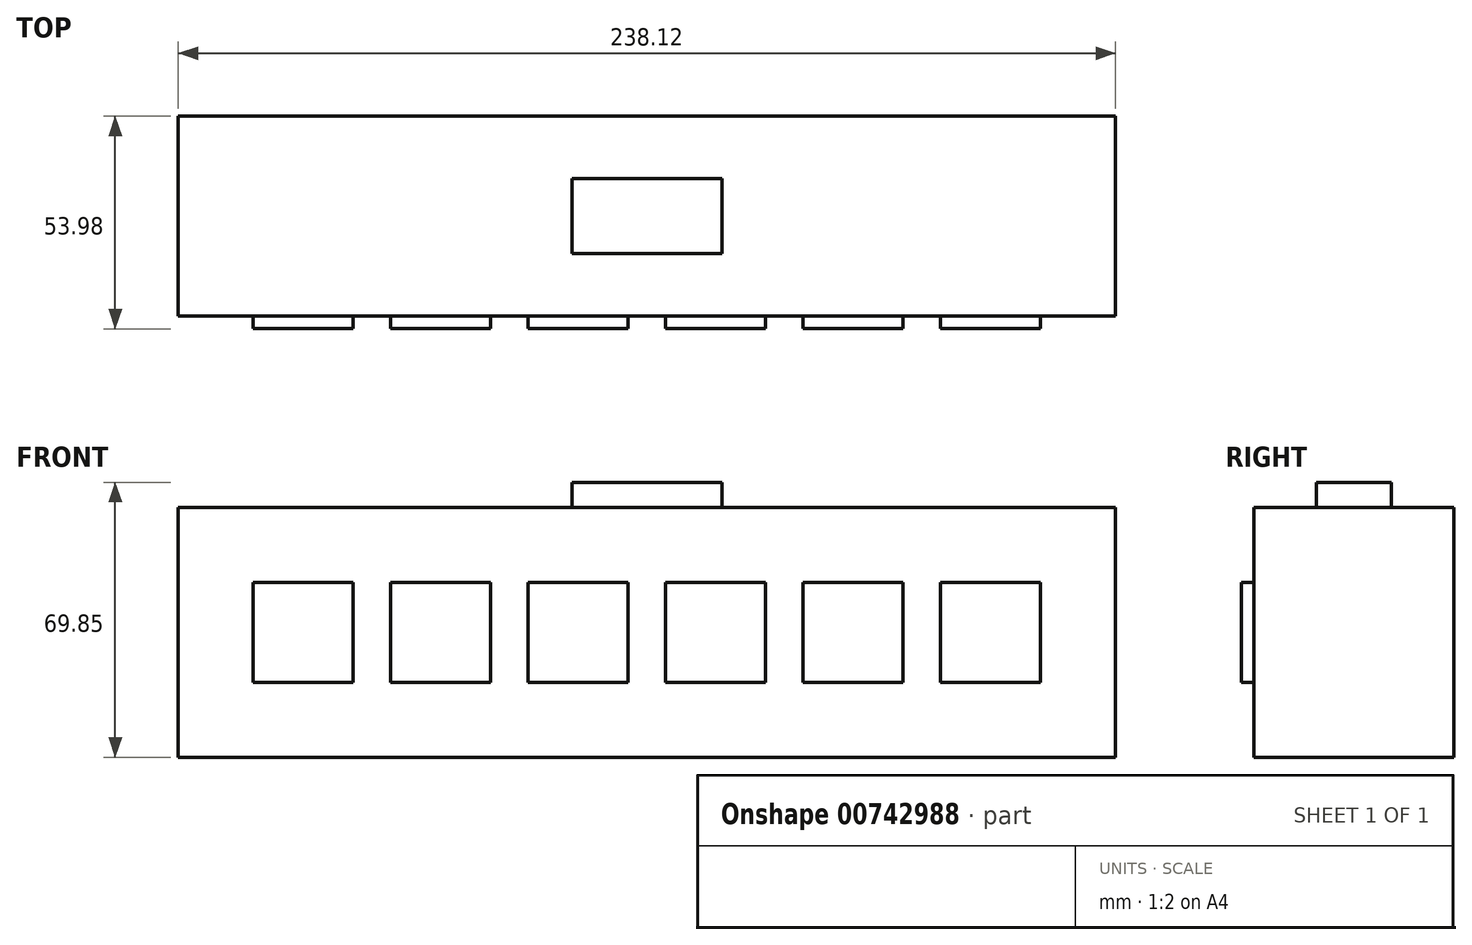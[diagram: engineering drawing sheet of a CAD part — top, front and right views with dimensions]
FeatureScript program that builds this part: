
annotation { "Feature Type Name" : "Feature", "Feature Type Description" : "" }
export const myFeature = defineFeature(function(context is Context, id is Id, definition is map)
    precondition{}
    {
        {
            var Q0;
            Q0=qCreatedBy(makeId("Front.planeOp"),FACE);
            var sketch = newSketch(context, id + "F0", { "sketchPlane" : qUnion([Q0])});
            skLineSegment(sketch, "E0.bottom", {"start": v(119.06, 31.75) * mm, "end": v(-119.06, 31.75) * mm});
            skLineSegment(sketch, "E0.top", {"start": v(119.06, -31.75) * mm, "end": v(-119.06, -31.75) * mm});
            skLineSegment(sketch, "E0.left", {"start": v(119.06, 31.75) * mm, "end": v(119.06, -31.75) * mm});
            skLineSegment(sketch, "E0.right", {"start": v(-119.06, 31.75) * mm, "end": v(-119.06, -31.75) * mm});
            skPoint(sketch, "E0.middle", {"position": v(0, 0) * mm});
            skSolve(sketch);
        }
        {
            var Q0;
            Q0=makeQuery(id+"F0.imprint","IMPRINT",FACE,{"disambiguationData":[TD([[makeQuery(id+"F0.imprint","IMPRINT",EDGE,{"derivedFrom":sQuery(id+"F0.wireOp",EDGE,"E0.bottom")}),1.0]])]});
            extrude(context, id + "F1", {"entities" : qUnion([Q0]), "depth" : 50.8 * mm, "offsetDistance" : 25.4 * mm});
        }
        {
            var Q0;
            Q0=makeQuery(id+"F1.opExtrude","CAP_FACE",FACE,{"disambiguationData":[OSD([sQuery(id+"F0.wireOp",EDGE,"E0.bottom"),sQuery(id+"F0.wireOp",EDGE,"E0.top"),sQuery(id+"F0.wireOp",EDGE,"E0.left"),sQuery(id+"F0.wireOp",EDGE,"E0.right")])],"isStart":false});
            var sketch = newSketch(context, id + "F2", { "sketchPlane" : qUnion([Q0])});
            skLineSegment(sketch, "E1", {"start": v(-119.06, 0) * mm, "end": v(-100.01, 0) * mm});
            skLineSegment(sketch, "E2", {"start": v(-100.01, 0) * mm, "end": v(-87.31, 0) * mm});
            skLineSegment(sketch, "E3", {"start": v(-87.31, 0) * mm, "end": v(-52.39, 0) * mm});
            skLineSegment(sketch, "E4", {"start": v(-52.39, 0) * mm, "end": v(-17.46, 0) * mm});
            skLineSegment(sketch, "E5", {"start": v(-17.46, 0) * mm, "end": v(17.46, 0) * mm});
            skLineSegment(sketch, "E6", {"start": v(17.46, 0) * mm, "end": v(52.39, 0) * mm});
            skLineSegment(sketch, "E7", {"start": v(52.39, 0) * mm, "end": v(87.31, 0) * mm});
            skLineSegment(sketch, "E8", {"start": v(87.31, 0) * mm, "end": v(100.01, 0) * mm});
            skLineSegment(sketch, "E9.bottom", {"start": v(-100.01, 12.7) * mm, "end": v(-74.61, 12.7) * mm});
            skLineSegment(sketch, "E9.top", {"start": v(-100.01, -12.7) * mm, "end": v(-74.61, -12.7) * mm});
            skLineSegment(sketch, "E9.left", {"start": v(-100.01, 12.7) * mm, "end": v(-100.01, -12.7) * mm});
            skLineSegment(sketch, "E9.right", {"start": v(-74.61, 12.7) * mm, "end": v(-74.61, -12.7) * mm});
            skPoint(sketch, "E9.middle", {"position": v(-87.31, 0) * mm});
            skLineSegment(sketch, "E10.bottom", {"start": v(-65.09, 12.7) * mm, "end": v(-39.69, 12.7) * mm});
            skLineSegment(sketch, "E10.top", {"start": v(-65.09, -12.7) * mm, "end": v(-39.69, -12.7) * mm});
            skLineSegment(sketch, "E10.left", {"start": v(-65.09, 12.7) * mm, "end": v(-65.09, -12.7) * mm});
            skLineSegment(sketch, "E10.right", {"start": v(-39.69, 12.7) * mm, "end": v(-39.69, -12.7) * mm});
            skPoint(sketch, "E10.middle", {"position": v(-52.39, 0) * mm});
            skLineSegment(sketch, "E11.bottom", {"start": v(-4.76, 12.7) * mm, "end": v(-30.16, 12.7) * mm});
            skLineSegment(sketch, "E11.top", {"start": v(-4.76, -12.7) * mm, "end": v(-30.16, -12.7) * mm});
            skLineSegment(sketch, "E11.left", {"start": v(-4.76, 12.7) * mm, "end": v(-4.76, -12.7) * mm});
            skLineSegment(sketch, "E11.right", {"start": v(-30.16, 12.7) * mm, "end": v(-30.16, -12.7) * mm});
            skPoint(sketch, "E11.middle", {"position": v(-17.46, 0) * mm});
            skLineSegment(sketch, "E12.bottom", {"start": v(30.16, 12.7) * mm, "end": v(4.76, 12.7) * mm});
            skLineSegment(sketch, "E12.top", {"start": v(30.16, -12.7) * mm, "end": v(4.76, -12.7) * mm});
            skLineSegment(sketch, "E12.left", {"start": v(30.16, 12.7) * mm, "end": v(30.16, -12.7) * mm});
            skLineSegment(sketch, "E12.right", {"start": v(4.76, 12.7) * mm, "end": v(4.76, -12.7) * mm});
            skPoint(sketch, "E12.middle", {"position": v(17.46, 0) * mm});
            skLineSegment(sketch, "E13.bottom", {"start": v(65.09, 12.7) * mm, "end": v(39.69, 12.7) * mm});
            skLineSegment(sketch, "E13.top", {"start": v(65.09, -12.7) * mm, "end": v(39.69, -12.7) * mm});
            skLineSegment(sketch, "E13.left", {"start": v(65.09, 12.7) * mm, "end": v(65.09, -12.7) * mm});
            skLineSegment(sketch, "E13.right", {"start": v(39.69, 12.7) * mm, "end": v(39.69, -12.7) * mm});
            skPoint(sketch, "E13.middle", {"position": v(52.39, 0) * mm});
            skLineSegment(sketch, "E14.bottom", {"start": v(100.01, 12.7) * mm, "end": v(74.61, 12.7) * mm});
            skLineSegment(sketch, "E14.top", {"start": v(100.01, -12.7) * mm, "end": v(74.61, -12.7) * mm});
            skLineSegment(sketch, "E14.left", {"start": v(100.01, 12.7) * mm, "end": v(100.01, -12.7) * mm});
            skLineSegment(sketch, "E14.right", {"start": v(74.61, 12.7) * mm, "end": v(74.61, -12.7) * mm});
            skPoint(sketch, "E14.middle", {"position": v(87.31, 0) * mm});
            skSolve(sketch);
        }
        {
            var Q0;
            {var subQ2=sQuery(id+"F2.wireOp",EDGE,"E2");Q0=makeQuery(id+"F2.imprint","IMPRINT",FACE,{"disambiguationData":[TD([[makeQuery(id+"F2.imprint","IMPRINT",EDGE,{"derivedFrom":subQ2}),-1.0]])]});}
            var Q1;
            {var subQ1=sQuery(id+"F2.wireOp",EDGE,"E2");Q1=makeQuery(id+"F2.imprint","IMPRINT",FACE,{"disambiguationData":[TD([[makeQuery(id+"F2.imprint","IMPRINT",EDGE,{"derivedFrom":subQ1}),1.0]])]});}
            var Q2;
            {var subQ1=sQuery(id+"F2.wireOp",EDGE,"E10.bottom");Q2=makeQuery(id+"F2.imprint","IMPRINT",FACE,{"disambiguationData":[TD([[makeQuery(id+"F2.imprint","IMPRINT",EDGE,{"derivedFrom":subQ1}),-1.0]])]});}
            var Q3;
            {var subQ1=sQuery(id+"F2.wireOp",EDGE,"E10.top");Q3=makeQuery(id+"F2.imprint","IMPRINT",FACE,{"disambiguationData":[TD([[makeQuery(id+"F2.imprint","IMPRINT",EDGE,{"derivedFrom":subQ1}),1.0]])]});}
            var Q4;
            {var subQ1=sQuery(id+"F2.wireOp",EDGE,"E11.bottom");Q4=makeQuery(id+"F2.imprint","IMPRINT",FACE,{"disambiguationData":[TD([[makeQuery(id+"F2.imprint","IMPRINT",EDGE,{"derivedFrom":subQ1}),1.0]])]});}
            var Q5;
            {var subQ1=sQuery(id+"F2.wireOp",EDGE,"E11.top");Q5=makeQuery(id+"F2.imprint","IMPRINT",FACE,{"disambiguationData":[TD([[makeQuery(id+"F2.imprint","IMPRINT",EDGE,{"derivedFrom":subQ1}),-1.0]])]});}
            var Q6;
            {var subQ0=sQuery(id+"F2.wireOp",EDGE,"E12.bottom");Q6=makeQuery(id+"F2.imprint","IMPRINT",FACE,{"disambiguationData":[TD([[makeQuery(id+"F2.imprint","IMPRINT",EDGE,{"derivedFrom":subQ0}),1.0]])]});}
            var Q7;
            {var subQ1=sQuery(id+"F2.wireOp",EDGE,"E12.top");Q7=makeQuery(id+"F2.imprint","IMPRINT",FACE,{"disambiguationData":[TD([[makeQuery(id+"F2.imprint","IMPRINT",EDGE,{"derivedFrom":subQ1}),-1.0]])]});}
            var Q8;
            {var subQ0=sQuery(id+"F2.wireOp",EDGE,"E13.bottom");Q8=makeQuery(id+"F2.imprint","IMPRINT",FACE,{"disambiguationData":[TD([[makeQuery(id+"F2.imprint","IMPRINT",EDGE,{"derivedFrom":subQ0}),1.0]])]});}
            var Q9;
            {var subQ0=sQuery(id+"F2.wireOp",EDGE,"E13.top");Q9=makeQuery(id+"F2.imprint","IMPRINT",FACE,{"disambiguationData":[TD([[makeQuery(id+"F2.imprint","IMPRINT",EDGE,{"derivedFrom":subQ0}),-1.0]])]});}
            var Q10;
            {var subQ1=sQuery(id+"F2.wireOp",EDGE,"E8");Q10=makeQuery(id+"F2.imprint","IMPRINT",FACE,{"disambiguationData":[TD([[makeQuery(id+"F2.imprint","IMPRINT",EDGE,{"derivedFrom":subQ1}),1.0]])]});}
            var Q11;
            {var subQ1=sQuery(id+"F2.wireOp",EDGE,"E8");Q11=makeQuery(id+"F2.imprint","IMPRINT",FACE,{"disambiguationData":[TD([[makeQuery(id+"F2.imprint","IMPRINT",EDGE,{"derivedFrom":subQ1}),-1.0]])]});}
            extrude(context, id + "F3", {"entities" : qUnion([Q0, Q1, Q2, Q3, Q4, Q5, Q6, Q7, Q8, Q9, Q10, Q11]), "operationType" : NewBodyOperationType.ADD, "depth" : 3.17 * mm, "offsetDistance" : 25.4 * mm});
        }
        {
            var Q0;
            Q0=makeQuery(id+"F1.opExtrude","SWEPT_FACE",FACE,{"disambiguationData":[OSD([sQuery(id+"F0.wireOp",EDGE,"E0.bottom")])]});
            var sketch = newSketch(context, id + "F4", { "sketchPlane" : qUnion([Q0])});
            skLineSegment(sketch, "E15.bottom", {"start": v(19.05, -15.88) * mm, "end": v(-19.05, -15.88) * mm});
            skLineSegment(sketch, "E15.top", {"start": v(19.05, -34.93) * mm, "end": v(-19.05, -34.93) * mm});
            skLineSegment(sketch, "E15.left", {"start": v(19.05, -15.88) * mm, "end": v(19.05, -34.93) * mm});
            skLineSegment(sketch, "E15.right", {"start": v(-19.05, -15.88) * mm, "end": v(-19.05, -34.93) * mm});
            skPoint(sketch, "E15.middle", {"position": v(0, -25.4) * mm});
            skPoint(sketch, "E15.middle.positionSnap0", {"position": v(119.06, -25.4) * mm});
            skPoint(sketch, "E15.centerSnap0", {"position": v(119.06, -25.4) * mm});
            skSolve(sketch);
        }
        {
            var Q0;
            Q0=makeQuery(id+"F4.imprint","IMPRINT",FACE,{"disambiguationData":[TD([[makeQuery(id+"F4.imprint","IMPRINT",EDGE,{"derivedFrom":sQuery(id+"F4.wireOp",EDGE,"E15.bottom")}),1.0]])]});
            extrude(context, id + "F5", {"entities" : qUnion([Q0]), "operationType" : NewBodyOperationType.ADD, "depth" : 6.35 * mm, "offsetDistance" : 25.4 * mm});
        }
    });
